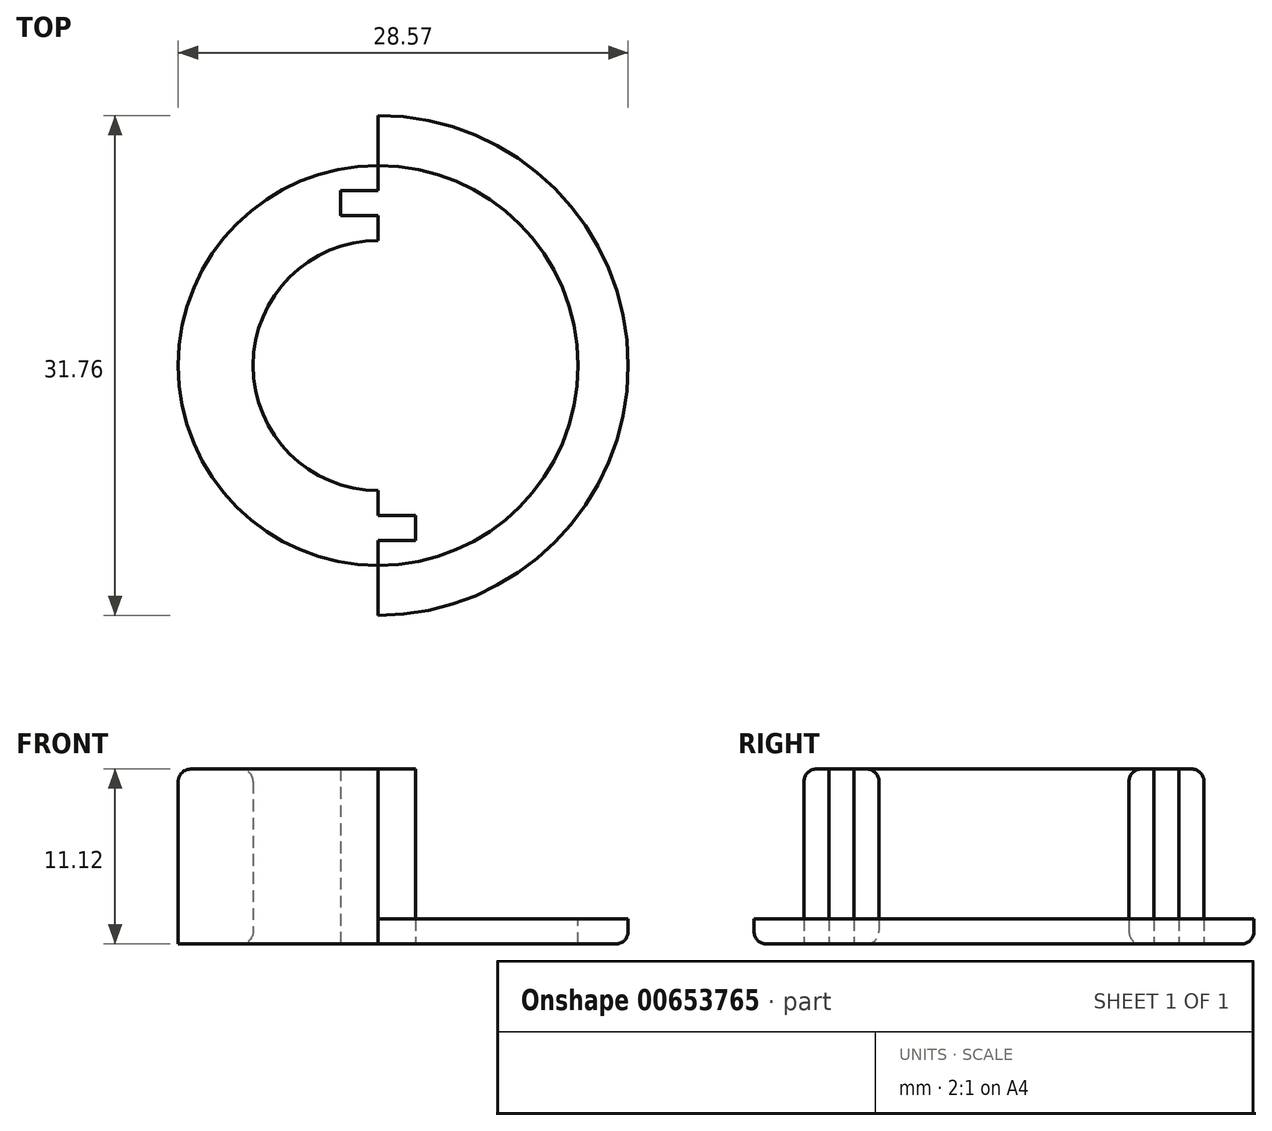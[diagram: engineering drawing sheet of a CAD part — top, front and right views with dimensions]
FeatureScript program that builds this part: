
annotation { "Feature Type Name" : "Feature", "Feature Type Description" : "" }
export const myFeature = defineFeature(function(context is Context, id is Id, definition is map)
    precondition{}
    {
        {
            var Q0;
            Q0=qCreatedBy(makeId("Top.planeOp"),FACE);
            var sketch = newSketch(context, id + "F0", { "sketchPlane" : qUnion([Q0])});
            skCircle(sketch, "E0", {"center": v(0, 0) * mm, "radius": 7.94 * mm});
            skCircle(sketch, "E1", {"center": v(0, 0) * mm, "radius": 12.7 * mm});
            skCircle(sketch, "E2", {"center": v(0, 0) * mm, "radius": 15.88 * mm});
            skLineSegment(sketch, "E3.bottom", {"start": v(0, 41.4) * mm, "end": v(56.47, 41.4) * mm});
            skLineSegment(sketch, "E3.top", {"start": v(0, -44.1) * mm, "end": v(56.47, -44.1) * mm});
            skLineSegment(sketch, "E3.left", {"start": v(0, 41.4) * mm, "end": v(0, -44.1) * mm});
            skLineSegment(sketch, "E3.right", {"start": v(56.47, 41.4) * mm, "end": v(56.47, -44.1) * mm});
            skLineSegment(sketch, "E4", {"start": v(0, 7.94) * mm, "end": v(0, 12.7) * mm, "construction": true});
            skLineSegment(sketch, "E5", {"start": v(0, -7.94) * mm, "end": v(0, -12.7) * mm});
            skLineSegment(sketch, "E6", {"start": v(0, -12.7) * mm, "end": v(0, -7.94) * mm, "construction": true});
            skLineSegment(sketch, "E7.bottom", {"start": v(2.38, -9.53) * mm, "end": v(-2.38, -9.53) * mm});
            skLineSegment(sketch, "E7.top", {"start": v(2.38, -11.11) * mm, "end": v(-2.38, -11.11) * mm});
            skLineSegment(sketch, "E7.left", {"start": v(2.38, -9.53) * mm, "end": v(2.38, -11.11) * mm});
            skLineSegment(sketch, "E7.right", {"start": v(-2.38, -9.53) * mm, "end": v(-2.38, -11.11) * mm});
            skPoint(sketch, "E7.middle", {"position": v(0, -10.32) * mm});
            skLineSegment(sketch, "E8", {"start": v(0, 0) * mm, "end": v(36.3, 0) * mm, "construction": true});
            skLineSegment(sketch, "E9.MirrorCS", {"start": v(2.38, 9.53) * mm, "end": v(-2.38, 9.53) * mm});
            skLineSegment(sketch, "E10.MirrorCS", {"start": v(-2.38, 9.53) * mm, "end": v(-2.38, 11.11) * mm});
            skLineSegment(sketch, "E11.MirrorCS", {"start": v(2.38, 11.11) * mm, "end": v(-2.38, 11.11) * mm});
            skLineSegment(sketch, "E12.MirrorCS", {"start": v(2.38, 9.53) * mm, "end": v(2.38, 11.11) * mm});
            skSolve(sketch);
        }
        {
            var Q0;
            {var subQ0=sQuery(id+"F0.wireOp",EDGE,"E7.right");Q0=makeQuery(id+"F0.imprint","IMPRINT",FACE,{"disambiguationData":[TD([[makeQuery(id+"F0.imprint","IMPRINT",EDGE,{"derivedFrom":subQ0}),-1.0]])]});}
            var Q1;
            {var subQ5=sQuery(id+"F0.wireOp",EDGE,"E7.right");Q1=makeQuery(id+"F0.imprint","IMPRINT",FACE,{"disambiguationData":[TD([[makeQuery(id+"F0.imprint","IMPRINT",EDGE,{"derivedFrom":subQ5}),1.0]])]});}
            var Q2;
            {var subQ5=sQuery(id+"F0.wireOp",EDGE,"E7.left");Q2=makeQuery(id+"F0.imprint","IMPRINT",FACE,{"disambiguationData":[TD([[makeQuery(id+"F0.imprint","IMPRINT",EDGE,{"derivedFrom":subQ5}),-1.0]])]});}
            extrude(context, id + "F1", {"entities" : qUnion([Q0, Q1, Q2]), "depth" : 9.52 * mm, "hasSecondDirection" : true, "secondDirectionOppositeDirection" : true, "secondDirectionDepth" : 1.59 * mm});
        }
        {
            var Q0;
            Q0=makeQuery(id+"F0.imprint","IMPRINT",FACE,{"disambiguationData":[TD([[makeQuery(id+"F0.imprint","IMPRINT",EDGE,{"derivedFrom":sQuery(id+"F0.wireOp",EDGE,"E1")}),-1.0]])]});
            extrude(context, id + "F2", {"entities" : qUnion([Q0]), "oppositeDirection" : true, "depth" : 1.59 * mm});
        }
        {
            var Q0;
            Q0=makeQuery(id+"F1.opExtrude","CAP_EDGE",EDGE,{"disambiguationData":[OSD([sQuery(id+"F0.wireOp",EDGE,"E1")])],"isStart":false});
            var Q1;
            Q1=makeQuery(id+"F1.opExtrude","CAP_EDGE",EDGE,{"disambiguationData":[OSD([sQuery(id+"F0.wireOp",EDGE,"E0")])],"isStart":false});
            var Q2;
            Q2=makeQuery(id+"F2.opExtrude","CAP_EDGE",EDGE,{"disambiguationData":[OSD([sQuery(id+"F0.wireOp",EDGE,"E2")])],"isStart":false});
            var Q3;
            Q3=makeQuery(id+"F1.opExtrude","CAP_EDGE",EDGE,{"disambiguationData":[OSD([sQuery(id+"F0.wireOp",EDGE,"E0")])],"isStart":true});
            fillet(context, id + "F3", {"entities" : qUnion([Q0, Q1, Q2, Q3]), "radius" : 0.8 * mm, "tangentPropagation" : true, "allowEdgeOverflow" : false});
        }
        {
            var Q0;
            {var subQ0=sQuery(id+"F0.wireOp",EDGE,"E3.left");var subQ1=sQuery(id+"F0.wireOp",EDGE,"E0");var subQ2=makeQuery(id+"F0.imprint","INTERSECT",VERTEX,{"disambiguationData":[OD(0.0)],"derivedFrom":[subQ1,subQ0]});Q0=makeQuery(id+"F0.imprint","IMPRINT",FACE,{"disambiguationData":[TD([[makeQuery(id+"F0.imprint","IMPRINT",EDGE,{"disambiguationData":[TD([[subQ2,1.0]])],"derivedFrom":subQ1}),-1.0]])]});}
            var Q1;
            {var subQ0=sQuery(id+"F0.wireOp",EDGE,"E3.left");var subQ1=sQuery(id+"F0.wireOp",EDGE,"E1");var subQ2=makeQuery(id+"F0.imprint","INTERSECT",VERTEX,{"disambiguationData":[OD(0.0)],"derivedFrom":[subQ1,subQ0]});Q1=makeQuery(id+"F0.imprint","IMPRINT",FACE,{"disambiguationData":[TD([[makeQuery(id+"F0.imprint","IMPRINT",EDGE,{"disambiguationData":[TD([[subQ2,1.0]])],"derivedFrom":subQ1}),-1.0]])]});}
            extrude(context, id + "F4", {"entities" : qUnion([Q0, Q1]), "operationType" : NewBodyOperationType.REMOVE, "depth" : 25.4 * mm, "hasSecondDirection" : true, "secondDirectionOppositeDirection" : true, "secondDirectionDepth" : 25.4 * mm});
        }
    });
